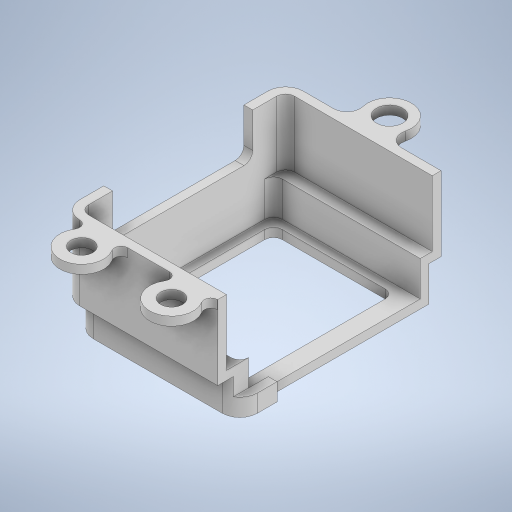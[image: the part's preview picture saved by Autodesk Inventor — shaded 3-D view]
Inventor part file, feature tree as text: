
AUTODESK INVENTOR PART (.ipt)
format: ipt  version: 2023 (Build 270158000, 158)  size: 475,136 bytes
history: native  units: in
note: dims shown in document units (in); Inventor stores cm internally (conversion verified against a paired STEP export)
features: extrude x8, sketch x5, projected_geometry x2, plane x1
ambient origin geometry x8: Origin, YZ Plane, XZ Plane, XY Plane, X Axis, Y Axis, Z Axis, Center Point
bodies: Body1 (feature_tree)
feature tree (16):
  extrude  "Extrusion3"  Depth=0.0787in
  plane  "Work Plane1"
  extrude  "Extrusion4"  Depth=0.315in TaperAngle=0.0deg
  sketch  "Sketch2"  dims[d8=0.0787in d9=0.0787in]
  extrude  "Extrusion7"  Depth=0.0787in
  extrude  "Extrusion8"  Depth=1.2402in
  extrude  "Extrusion10"  Depth=1.2402in
  extrude  "Extrusion11"  Depth=0.0787in TaperAngle=0.0deg
  extrude  "Extrusion12"  Depth=0.5906in TaperAngle=0.0deg
  extrude  "Extrusion13"  Depth=0.3937in
  projected_geometry  "Projected Loop1"
  sketch  "Sketch5"  dims[d10=0.0787in d11=0.0in d12=0.315in d13=0.0in]
  sketch  "Sketch6"  dims[d14=0.315in d19=0.0787in]
  projected_geometry  "Projected Loop3"
  sketch  "Sketch7"  dims[d20=0.0787in d21=1.2402in]
  sketch  "Sketch8"  dims[d22=1.2402in d23=1.2402in d28=0.0787in d29=0.0in d30=0.5906in d31=0.0in d34=0.3937in d35=0.2362in d38=0.1181in d39=0.1181in d40=0.3937in d41=0.1969in d42=0.1181in d43=0.1181in d44=0.3937in d45=0.1969in d46=0.1181in d47=0.1181in d49=0.8071in d50=0.0787in d51=0.0in d52=0.1575in d53=1.4646in d54=1.0827in d55=0.1575in d56=0.0787in d57=0.0787in d58=0.0in d59=0.0787in d61=1.2598in d62=1.6929in d64=0.2362in d65=0.0in d66=0.0787in d67=0.0787in d68=0.1772in d69=0.1575in d70=0.2362in d71=0.0in]
